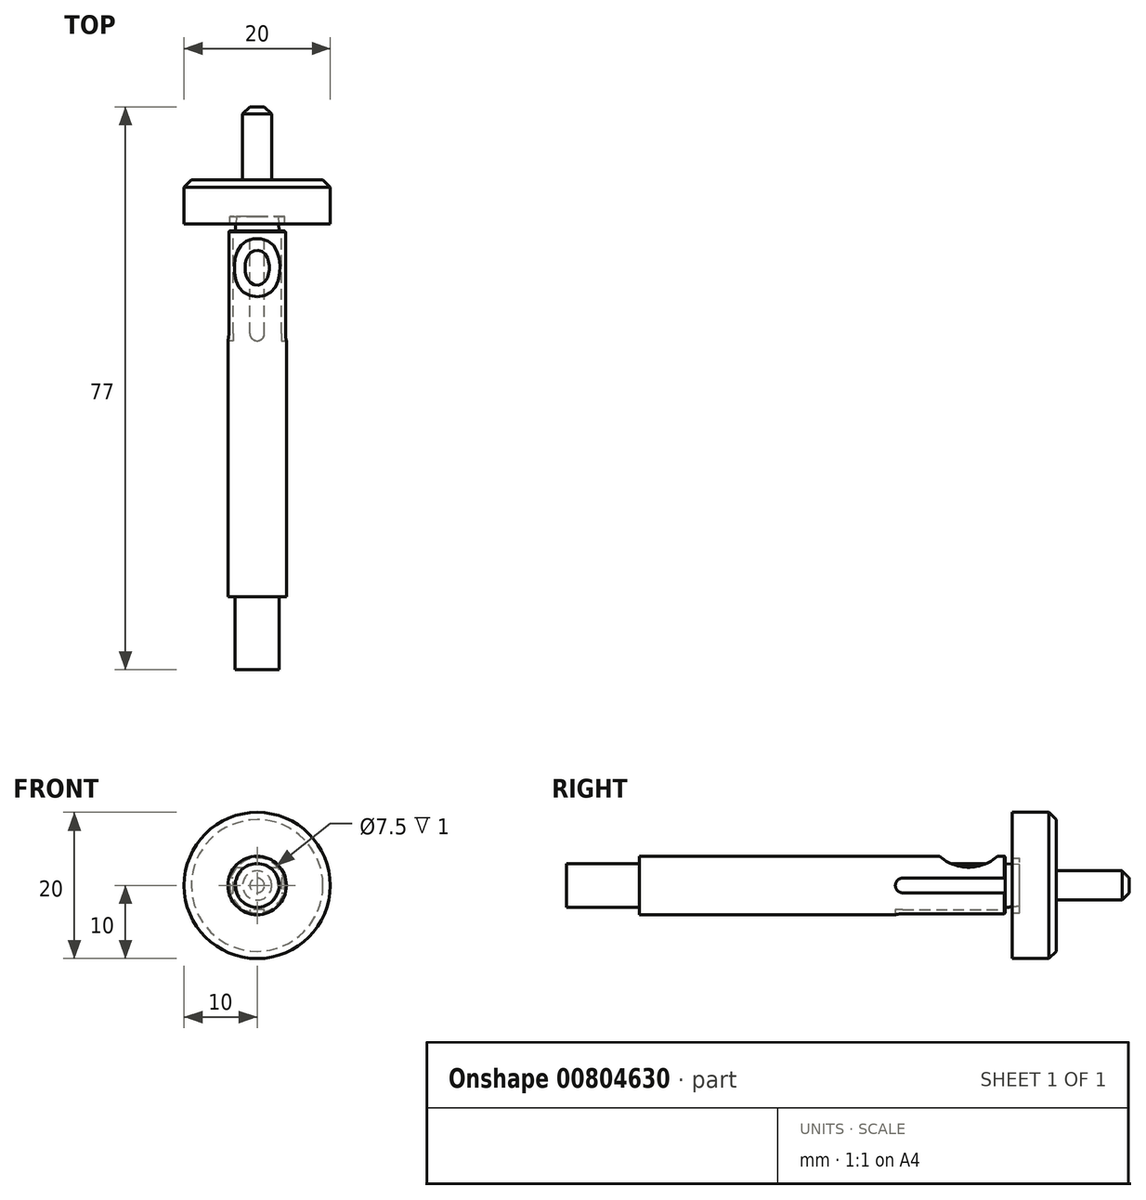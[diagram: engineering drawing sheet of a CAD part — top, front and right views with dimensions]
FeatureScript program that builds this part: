
annotation { "Feature Type Name" : "Feature", "Feature Type Description" : "" }
export const myFeature = defineFeature(function(context is Context, id is Id, definition is map)
    precondition{}
    {
        {
            var Q0;
            Q0=qCreatedBy(makeId("Front.planeOp"),FACE);
            var sketch = newSketch(context, id + "F0", { "sketchPlane" : qUnion([Q0])});
            skCircle(sketch, "E0", {"center": v(0, 0) * mm, "radius": 4 * mm});
            skCircle(sketch, "E1", {"center": v(0, 0) * mm, "radius": 3 * mm});
            skSolve(sketch);
        }
        {
            var Q0;
            Q0 = qSketchRegion(id + "F0", true);
            extrude(context, id + "F1", {"entities" : qUnion([Q0]), "depth" : 50 * mm, "offsetDistance" : 25 * mm});
        }
        {
            var Q0;
            Q0=qCreatedBy(makeId("Right.planeOp"),FACE);
            var sketch = newSketch(context, id + "F2", { "sketchPlane" : qUnion([Q0])});
            skCircle(sketch, "E2", {"center": v(-5, 8.5) * mm, "radius": 6 * mm});
            skSolve(sketch);
        }
        {
            var Q0;
            Q0 = qSketchRegion(id + "F2", true);
            extrude(context, id + "F3", {"entities" : qUnion([Q0]), "operationType" : NewBodyOperationType.REMOVE, "oppositeDirection" : true, "depth" : 25 * mm, "offsetDistance" : 25 * mm, "hasSecondDirection" : true, "secondDirectionOppositeDirection" : false, "secondDirectionDepth" : 25 * mm});
        }
        {
            var Q0;
            Q0=makeQuery(id+"F1.opExtrude","CAP_FACE",FACE,{"disambiguationData":[OSD([sQuery(id+"F0.wireOp",EDGE,"E0"),sQuery(id+"F0.wireOp",EDGE,"E1")])],"isStart":true});
            var sketch = newSketch(context, id + "F4", { "sketchPlane" : qUnion([Q0])});
            skLineSegment(sketch, "E3", {"start": v(-4.3, 0) * mm, "end": v(-4.3, 1) * mm});
            skLineSegment(sketch, "E4", {"start": v(-4.3, 1) * mm, "end": v(-3.3, 1) * mm});
            skLineSegment(sketch, "E5", {"start": v(-3.3, 1) * mm, "end": v(-3.3, -1) * mm});
            skLineSegment(sketch, "E6", {"start": v(-3.3, -1) * mm, "end": v(-4.3, -1) * mm});
            skLineSegment(sketch, "E7", {"start": v(-4.3, -1) * mm, "end": v(-4.3, 0) * mm});
            skLineSegment(sketch, "E8.1.0", {"start": v(-1, -3.3) * mm, "end": v(1, -3.3) * mm});
            skLineSegment(sketch, "E8.1.1", {"start": v(-1, -4.3) * mm, "end": v(-1, -3.3) * mm});
            skLineSegment(sketch, "E8.1.2", {"start": v(0, -4.3) * mm, "end": v(-1, -4.3) * mm});
            skLineSegment(sketch, "E8.1.3", {"start": v(1, -4.3) * mm, "end": v(0, -4.3) * mm});
            skLineSegment(sketch, "E8.1.4", {"start": v(1, -3.3) * mm, "end": v(1, -4.3) * mm});
            skLineSegment(sketch, "E8.2.0", {"start": v(3.3, -1) * mm, "end": v(3.3, 1) * mm});
            skLineSegment(sketch, "E8.2.1", {"start": v(4.3, -1) * mm, "end": v(3.3, -1) * mm});
            skLineSegment(sketch, "E8.2.2", {"start": v(4.3, 0) * mm, "end": v(4.3, -1) * mm});
            skLineSegment(sketch, "E8.2.3", {"start": v(4.3, 1) * mm, "end": v(4.3, 0) * mm});
            skLineSegment(sketch, "E8.2.4", {"start": v(3.3, 1) * mm, "end": v(4.3, 1) * mm});
            skPoint(sketch, "E8.center", {"position": v(0, 0) * mm});
            skSolve(sketch);
        }
        {
            var Q0;
            Q0 = qSketchRegion(id + "F4", true);
            extrude(context, id + "F5", {"entities" : qUnion([Q0]), "operationType" : NewBodyOperationType.REMOVE, "oppositeDirection" : true, "depth" : 15 * mm, "offsetDistance" : 25 * mm});
        }
        {
            var Q0;
            {var subQ0=sQuery(id+"F0.wireOp",EDGE,"E0");Q0=makeQuery(id+"F5.boolean.opBoolean","SPLIT",EDGE,{"disambiguationData":[TD([makeQuery(id+"F5.opExtrude","SWEPT_FACE",FACE,{"disambiguationData":[OSD([sQuery(id+"F4.wireOp",EDGE,"E4")])]})])],"derivedFrom":makeQuery(id+"F1.opExtrude","CAP_EDGE",EDGE,{"disambiguationData":[OSD([subQ0])],"isStart":true})});}
            var Q1;
            {var subQ0=sQuery(id+"F0.wireOp",EDGE,"E0");Q1=makeQuery(id+"F5.boolean.opBoolean","SPLIT",EDGE,{"disambiguationData":[TD([makeQuery(id+"F5.opExtrude","SWEPT_FACE",FACE,{"disambiguationData":[OSD([sQuery(id+"F4.wireOp",EDGE,"E6")])]})])],"derivedFrom":makeQuery(id+"F1.opExtrude","CAP_EDGE",EDGE,{"disambiguationData":[OSD([subQ0])],"isStart":true})});}
            var Q2;
            {var subQ0=sQuery(id+"F0.wireOp",EDGE,"E0");Q2=makeQuery(id+"F5.boolean.opBoolean","SPLIT",EDGE,{"disambiguationData":[TD([makeQuery(id+"F5.opExtrude","SWEPT_FACE",FACE,{"disambiguationData":[OSD([sQuery(id+"F4.wireOp",EDGE,"E8.1.4")])]})])],"derivedFrom":makeQuery(id+"F1.opExtrude","CAP_EDGE",EDGE,{"disambiguationData":[OSD([subQ0])],"isStart":true})});}
            chamfer(context, id + "F6", {"entities" : qUnion([Q0, Q1, Q2]), "width" : 0.1 * mm, "tangentPropagation" : true});
        }
        {
            var Q0;
            Q0=makeQuery(id+"F5.boolean.opBoolean","COPY",EDGE,{"derivedFrom":makeQuery(id+"F5.opExtrude","CAP_EDGE",EDGE,{"disambiguationData":[OSD([sQuery(id+"F4.wireOp",EDGE,"E4")])],"isStart":false})});
            var Q1;
            Q1=makeQuery(id+"F5.boolean.opBoolean","COPY",EDGE,{"derivedFrom":makeQuery(id+"F5.opExtrude","CAP_EDGE",EDGE,{"disambiguationData":[OSD([sQuery(id+"F4.wireOp",EDGE,"E6")])],"isStart":false})});
            var Q2;
            Q2=makeQuery(id+"F5.boolean.opBoolean","COPY",EDGE,{"derivedFrom":makeQuery(id+"F5.opExtrude","CAP_EDGE",EDGE,{"disambiguationData":[OSD([sQuery(id+"F4.wireOp",EDGE,"E8.1.1")])],"isStart":false})});
            var Q3;
            Q3=makeQuery(id+"F5.boolean.opBoolean","COPY",EDGE,{"derivedFrom":makeQuery(id+"F5.opExtrude","CAP_EDGE",EDGE,{"disambiguationData":[OSD([sQuery(id+"F4.wireOp",EDGE,"E8.1.4")])],"isStart":false})});
            var Q4;
            Q4=makeQuery(id+"F5.boolean.opBoolean","COPY",EDGE,{"derivedFrom":makeQuery(id+"F5.opExtrude","CAP_EDGE",EDGE,{"disambiguationData":[OSD([sQuery(id+"F4.wireOp",EDGE,"E8.2.1")])],"isStart":false})});
            var Q5;
            Q5=makeQuery(id+"F5.boolean.opBoolean","COPY",EDGE,{"derivedFrom":makeQuery(id+"F5.opExtrude","CAP_EDGE",EDGE,{"disambiguationData":[OSD([sQuery(id+"F4.wireOp",EDGE,"E8.2.4")])],"isStart":false})});
            fillet(context, id + "F7", {"entities" : qUnion([Q0, Q1, Q2, Q3, Q4, Q5]), "radius" : 1 * mm, "tangentPropagation" : true, "allowEdgeOverflow" : false});
        }
        {
            var Q0;
            Q0=makeQuery(id+"F1.opExtrude","CAP_FACE",FACE,{"disambiguationData":[OSD([sQuery(id+"F0.wireOp",EDGE,"E0"),sQuery(id+"F0.wireOp",EDGE,"E1")])],"isStart":true});
            var sketch = newSketch(context, id + "F8", { "sketchPlane" : qUnion([Q0])});
            skCircle(sketch, "E9", {"center": v(0, 0) * mm, "radius": 3 * mm});
            skSolve(sketch);
        }
        {
            var Q0;
            Q0 = qSketchRegion(id + "F8", true);
            extrude(context, id + "F9", {"entities" : qUnion([Q0]), "operationType" : NewBodyOperationType.ADD, "depth" : 2 * mm, "offsetDistance" : 25 * mm, "hasSecondDirection" : true, "secondDirectionOppositeDirection" : true, "secondDirectionDepth" : 60 * mm});
        }
        {
            var Q0;
            Q0=makeQuery(id+"F9.opExtrude","CAP_EDGE",EDGE,{"disambiguationData":[OSD([sQuery(id+"F8.wireOp",EDGE,"E9")])],"isStart":false});
            chamfer(context, id + "F10", {"entities" : qUnion([Q0]), "chamferType" : ChamferType.OFFSET_ANGLE, "width" : 2 * mm, "oppositeDirection" : false, "angle" : 4 * degree, "tangentPropagation" : true});
        }
        {
            var Q0;
            Q0=makeQuery(id+"F9.opExtrude","CAP_FACE",FACE,{"disambiguationData":[OSD([sQuery(id+"F8.wireOp",EDGE,"E9")])],"isStart":false});
            var sketch = newSketch(context, id + "F11", { "sketchPlane" : qUnion([Q0])});
            skCircle(sketch, "E10", {"center": v(0, 0) * mm, "radius": 2.9 * mm});
            skSolve(sketch);
        }
        {
            var Q0;
            {var subQ0=sQuery(id+"F8.wireOp",EDGE,"E9");Q0=makeQuery(id+"F11.imprint","IMPRINT",FACE,{"disambiguationData":[TD([[makeQuery(id+"F11.imprint","IMPRINT",EDGE,{"derivedFrom":makeQuery(id+"F10.opChamfer","BLEND_EDGE",EDGE,{"blendedFrom":[makeQuery(id+"F9.opExtrude","CAP_EDGE",EDGE,{"disambiguationData":[OSD([subQ0])],"isStart":false}),makeQuery(id+"F9.opExtrude","CAP_FACE",FACE,{"disambiguationData":[OSD([subQ0])],"isStart":false})],"blendedInto":[makeQuery(id+"F9.opExtrude","CAP_FACE",FACE,{"disambiguationData":[OSD([subQ0])],"isStart":false})]})}),1.0]])]});}
            var sketch = newSketch(context, id + "F12", { "sketchPlane" : qUnion([Q0])});
            skCircle(sketch, "E11", {"center": v(0, 0) * mm, "radius": 2 * mm});
            skSolve(sketch);
        }
        {
            var Q0;
            Q0 = qSketchRegion(id + "F12", true);
            extrude(context, id + "F13", {"entities" : qUnion([Q0]), "operationType" : NewBodyOperationType.ADD, "depth" : 15 * mm, "offsetDistance" : 25 * mm});
        }
        {
            var Q0;
            Q0=makeQuery(id+"F13.opExtrude","CAP_EDGE",EDGE,{"disambiguationData":[OSD([sQuery(id+"F12.wireOp",EDGE,"E11")])],"isStart":false});
            chamfer(context, id + "F14", {"entities" : qUnion([Q0]), "width" : 1 * mm, "tangentPropagation" : true});
        }
        {
            var Q0;
            {var subQ0=sQuery(id+"F8.wireOp",EDGE,"E9");Q0=makeQuery(id+"F11.imprint","IMPRINT",FACE,{"disambiguationData":[TD([[makeQuery(id+"F11.imprint","IMPRINT",EDGE,{"derivedFrom":makeQuery(id+"F10.opChamfer","BLEND_EDGE",EDGE,{"blendedFrom":[makeQuery(id+"F9.opExtrude","CAP_EDGE",EDGE,{"disambiguationData":[OSD([subQ0])],"isStart":false}),makeQuery(id+"F9.opExtrude","CAP_FACE",FACE,{"disambiguationData":[OSD([subQ0])],"isStart":false})],"blendedInto":[makeQuery(id+"F9.opExtrude","CAP_FACE",FACE,{"disambiguationData":[OSD([subQ0])],"isStart":false})]})}),1.0]])]});}
            var sketch = newSketch(context, id + "F15", { "sketchPlane" : qUnion([Q0])});
            skCircle(sketch, "E12", {"center": v(0, 0) * mm, "radius": 10 * mm});
            skSolve(sketch);
        }
        {
            var Q0;
            Q0 = qSketchRegion(id + "F15", true);
            extrude(context, id + "F16", {"entities" : qUnion([Q0]), "operationType" : NewBodyOperationType.ADD, "depth" : 5 * mm, "offsetDistance" : 25 * mm});
        }
        {
            var Q0;
            Q0=makeQuery(id+"F16.opExtrude","CAP_FACE",FACE,{"disambiguationData":[OSD([sQuery(id+"F15.wireOp",EDGE,"E12")])],"isStart":true});
            var sketch = newSketch(context, id + "F17", { "sketchPlane" : qUnion([Q0])});
            skCircle(sketch, "E13", {"center": v(0, 0) * mm, "radius": 3.75 * mm});
            skCircle(sketch, "E14", {"center": v(0, 0) * mm, "radius": 10 * mm});
            skSolve(sketch);
        }
        {
            var Q0;
            Q0 = qSketchRegion(id + "F17", true);
            extrude(context, id + "F18", {"entities" : qUnion([Q0]), "operationType" : NewBodyOperationType.ADD, "depth" : 1 * mm, "offsetDistance" : 25 * mm});
        }
        {
            var Q0;
            Q0=makeQuery(id+"F18.opExtrude","CAP_FACE",FACE,{"disambiguationData":[OSD([sQuery(id+"F17.wireOp",EDGE,"E13"),sQuery(id+"F17.wireOp",EDGE,"E14")])],"isStart":false});
            var sketch = newSketch(context, id + "F19", { "sketchPlane" : qUnion([Q0])});
            skCircle(sketch, "E15", {"center": v(0, 0) * mm, "radius": 5 * mm});
            skCircle(sketch, "E16", {"center": v(0, 0) * mm, "radius": 10 * mm});
            skSolve(sketch);
        }
        {
            var Q0;
            Q0=makeQuery(id+"F8n4hqaE7jrRMnY_1.opExtrude","CAP_EDGE",EDGE,{"disambiguationData":[OSD([sQuery(id+"F19.wireOp",EDGE,"E16")])],"isStart":false});
            var Q1;
            Q1=makeQuery(id+"F16.opExtrude","CAP_EDGE",EDGE,{"disambiguationData":[OSD([sQuery(id+"F15.wireOp",EDGE,"E12")])],"isStart":false});
            chamfer(context, id + "F20", {"entities" : qUnion([Q0, Q1]), "width" : 1 * mm, "tangentPropagation" : true});
        }
    });
